# Revit family: Air Terminals_LDI-V_Anschlusskasten Typ AK
name_source: partatom
category: Air Terminals
revit_build: Autodesk Revit 2017 (Build: 20160225_1515(x64)
units: mm (PartAtom-declared; Revit-internal decimal feet)

## family parameters
Always vertical = Yes
Cut with Voids When Loaded = No
OmniClass Number = 23.40.40.14.21.11
OmniClass Title = Food Service Hoods
Part Type = Normal
Room Calculation Point = No
Round Connector Dimension = Use Diameter
Shared = No
Work Plane-Based = No

## types (18) — shared parameters
Lwa (dB(A)) = 40/50/60
Max Flow = 0.0 L/s
Maß K (nur LDI-V) mm = 8 mm  [stored 0.0262467 ft]
Min Flow = 0.0 L/s

## per-type parameters (varying)
| type | Bauhöhe L (nur EI/EA_nur TA/TB) mm | DN | Einbauhöhe (m) | L | Leaf_b | Masse (kg) SM_EI/ EA_TA/TB | Maß H mm | Maß Ø A mm | Maß Ø D1 | Maß Ø R mm | Maß Ø R1 mm | Mindestabstand (m) | Visible | Visible_DN | Vo (m3/h) | Ymax (m) | ∆p (Pa) |
| LDI-V/SM_DN 250 | 0 mm  [stored 0 ft] | 1 | 3.0/3.0/3.0 | 1 | 120 mm  [stored 0.393701 ft] | 2.7 | 140 mm  [stored 0.459318 ft] | 253 mm  [stored 0.830052 ft] | 223 mm  [stored 0.731627 ft] | 330 mm | 480 mm  [stored 1.5748 ft] | 2.0/2.8/3.9 | No | Yes | 410/580/810 | 2.5/3.7/5.5 | 31/61/119 |
| LDI-V/SM_DN 315 | 0 mm  [stored 0 ft] | 2 | 4.5/4.5/4.5 | 2 | 150 mm | 3.8 | 175 mm  [stored 0.574147 ft] | 318 mm  [stored 1.04331 ft] | 279 mm | 415 mm  [stored 1.36155 ft] | 580 mm  [stored 1.90289 ft] | 2.9/4.1/5.5 | No | Yes | 820/1150/1550 | 3.5/5.2/7.3 | 39/76/138 |
| LDI-V/SM_DN 400 | 0 mm  [stored 0 ft] | 3 | 6.0/6.0/6.0 | 3 | 190 mm | 6.3 | 215 mm | 403 mm  [stored 1.32218 ft] | 354 mm  [stored 1.16142 ft] | 535 mm  [stored 1.75525 ft] | 750 mm  [stored 2.46063 ft] | 3.3/4.6/6.5 | No | Yes | 1300/1800/2550 | 3.8/5.5/8.2 | 37/71/143 |
| LDI-V/SM_DN 500 | 0 mm  [stored 0 ft] | 4 | 8.0/8.0/8.0 | 4 | 239 mm  [stored 0.784121 ft] | 8.9 | 280 mm  [stored 0.918635 ft] | 503 mm  [stored 1.65026 ft] | 449 mm  [stored 1.4731 ft] | 660 mm | 925 mm | 3.6/5.0/7.1 | No | Yes | 1900/2650/3750 | 3.9/5.7/8.4 | 32/62/124 |
| LDI-V/SM_DN 630 | 0 mm  [stored 0 ft] | 5 | 10.0/10.0/10.0 | 5 | 300 mm  [stored 0.984252 ft] | 14.5 | 355 mm | 633 mm  [stored 2.07677 ft] | 559 mm  [stored 1.83399 ft] | 830 mm  [stored 2.7231 ft] | 1160 mm | 3.9/5.5/7.7 | No | Yes | 2800/3900/5500 | 4.0/5.8/8.6 | 27/53/104 |
| LDI-V/SM_DN 800 | 0 mm  [stored 0 ft] | 6 | 12.0/12.0/12.0 | 6 | 381 mm  [stored 1.25 ft] | 30.0 | 425 mm  [stored 1.39436 ft] | 804 mm  [stored 2.6378 ft] | 699 mm  [stored 2.29331 ft] | 1100 mm | 1420 mm | 4.4/6.1/8.4 | No | No | 4300/6000/8300 | 4.2/6.1/8.9 | 24/47/91 |
| LDI-V/EI_DN 250 | 285 mm  [stored 0.935039 ft] | 1 | 3.0/3.0/3.0 | 7 | 120 mm  [stored 0.393701 ft] | 4.1 | 140 mm  [stored 0.459318 ft] | 253 mm  [stored 0.830052 ft] | 223 mm  [stored 0.731627 ft] | 330 mm | 480 mm  [stored 1.5748 ft] | 2.0/2.8/3.9 | Yes | Yes | 410/580/810 | 2.5/3.7/5.5 | 31/61/119 |
| LDI-V/EI_DN 315 | 295 mm  [stored 0.967848 ft] | 2 | 4.5/4.5/4.5 | 8 | 150 mm | 5.3 | 175 mm  [stored 0.574147 ft] | 318 mm  [stored 1.04331 ft] | 279 mm | 415 mm  [stored 1.36155 ft] | 580 mm  [stored 1.90289 ft] | 2.9/4.1/5.5 | Yes | Yes | 820/1150/1550 | 3.5/5.2/7.3 | 39/76/138 |
| LDI-V/EI_DN 400 | 300 mm  [stored 0.984252 ft] | 3 | 6.0/6.0/6.0 | 9 | 190 mm | 7.0 | 215 mm | 403 mm  [stored 1.32218 ft] | 354 mm  [stored 1.16142 ft] | 535 mm  [stored 1.75525 ft] | 750 mm  [stored 2.46063 ft] | 3.3/4.6/6.5 | Yes | Yes | 1300/1800/2550 | 3.8/5.5/8.2 | 37/71/143 |
| LDI-V/EI_DN 500 | 325 mm  [stored 1.06627 ft] | 4 | 8.0/8.0/8.0 | 10 | 239 mm  [stored 0.784121 ft] | 10.2 | 280 mm  [stored 0.918635 ft] | 503 mm  [stored 1.65026 ft] | 449 mm  [stored 1.4731 ft] | 660 mm | 925 mm | 3.6/5.0/7.1 | Yes | Yes | 1900/2650/3750 | 3.9/5.7/8.4 | 32/62/124 |
| LDI-V/EI_DN 630 | 345 mm  [stored 1.13189 ft] | 5 | 10.0/10.0/10.0 | 11 | 300 mm  [stored 0.984252 ft] | 15.4 | 355 mm | 633 mm  [stored 2.07677 ft] | 559 mm  [stored 1.83399 ft] | 830 mm  [stored 2.7231 ft] | 1160 mm | 3.9/5.5/7.7 | Yes | Yes | 2800/3900/5500 | 4.0/5.8/8.6 | 27/53/104 |
| LDI-V/EI_DN 800 | 425 mm  [stored 1.39436 ft] | 6 | 12.0/12.0/12.0 | 12 | 381 mm  [stored 1.25 ft] | 31.2 | 425 mm  [stored 1.39436 ft] | 804 mm  [stored 2.6378 ft] | 699 mm  [stored 2.29331 ft] | 1100 mm | 1420 mm | 4.4/6.1/8.4 | Yes | No | 4300/6000/8300 | 4.2/6.1/8.9 | 24/47/91 |
| LDI-V/TA_DN 250 | 270 mm  [stored 0.885827 ft] | 1 | 3.0/3.0/3.0 | 13 | 120 mm  [stored 0.393701 ft] | 4.1 | 140 mm  [stored 0.459318 ft] | 253 mm  [stored 0.830052 ft] | 223 mm  [stored 0.731627 ft] | 330 mm | 480 mm  [stored 1.5748 ft] | 2.0/2.8/3.9 | Yes | Yes | 410/580/810 | 2.5/3.7/5.5 | 31/61/119 |
| LDI-V/TA_DN 315 | 280 mm  [stored 0.918635 ft] | 2 | 4.5/4.5/4.5 | 14 | 150 mm | 5.3 | 175 mm  [stored 0.574147 ft] | 318 mm  [stored 1.04331 ft] | 279 mm | 415 mm  [stored 1.36155 ft] | 580 mm  [stored 1.90289 ft] | 2.9/4.1/5.5 | Yes | Yes | 820/1150/1550 | 3.5/5.2/7.3 | 39/76/138 |
| LDI-V/TA_DN 400 | 290 mm  [stored 0.951444 ft] | 3 | 6.0/6.0/6.0 | 15 | 190 mm | 6.7 | 215 mm | 403 mm  [stored 1.32218 ft] | 354 mm  [stored 1.16142 ft] | 535 mm  [stored 1.75525 ft] | 750 mm  [stored 2.46063 ft] | 3.3/4.6/6.5 | Yes | Yes | 1300/1800/2550 | 3.8/5.5/8.2 | 37/71/143 |
| LDI-V/TA_DN 500 | 290 mm  [stored 0.951444 ft] | 4 | 8.0/8.0/8.0 | 16 | 239 mm  [stored 0.784121 ft] | 9.9 | 280 mm  [stored 0.918635 ft] | 503 mm  [stored 1.65026 ft] | 449 mm  [stored 1.4731 ft] | 660 mm | 925 mm | 3.6/5.0/7.1 | Yes | Yes | 1900/2650/3750 | 3.9/5.7/8.4 | 32/62/124 |
| LDI-V/TA_DN 630 | 355 mm | 5 | 10.0/10.0/10.0 | 17 | 300 mm  [stored 0.984252 ft] | 15.1 | 355 mm | 633 mm  [stored 2.07677 ft] | 559 mm  [stored 1.83399 ft] | 830 mm  [stored 2.7231 ft] | 1160 mm | 3.9/5.5/7.7 | Yes | Yes | 2800/3900/5500 | 4.0/5.8/8.6 | 27/53/104 |
| LDI-V/TA_DN 800 | 425 mm  [stored 1.39436 ft] | 6 | 12.0/12.0/12.0 | 18 | 381 mm  [stored 1.25 ft] | 30.2 | 425 mm  [stored 1.39436 ft] | 804 mm  [stored 2.6378 ft] | 699 mm  [stored 2.29331 ft] | 1100 mm | 1420 mm | 4.4/6.1/8.4 | Yes | No | 4300/6000/8300 | 4.2/6.1/8.9 | 24/47/91 |

note: [stored X ft] marks values corroborated as IEEE doubles in the binary element streams (Revit-internal decimal feet)

## geometry (parser evidence)
native form markers: Sweep x20
no freeform markers — native parametric forms only
